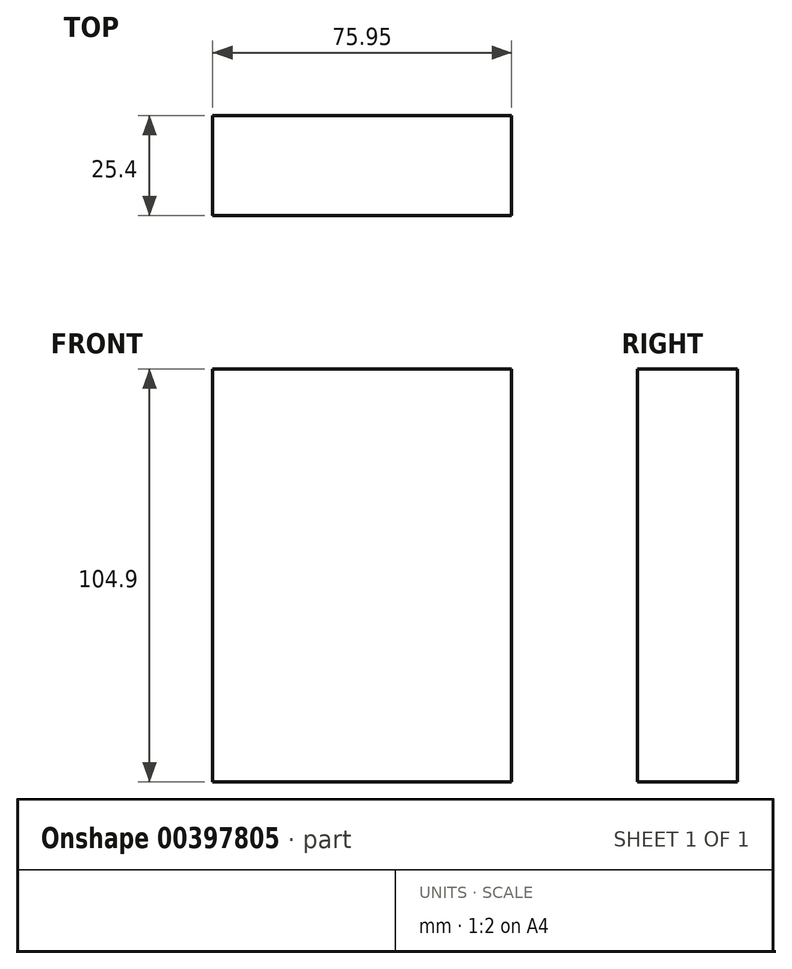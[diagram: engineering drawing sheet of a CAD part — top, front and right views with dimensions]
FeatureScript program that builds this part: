
annotation { "Feature Type Name" : "Feature", "Feature Type Description" : "" }
export const myFeature = defineFeature(function(context is Context, id is Id, definition is map)
    precondition{}
    {
        {
            var Q0;
            Q0=qCreatedBy(makeId("Front.planeOp"),FACE);
            var sketch = newSketch(context, id + "F0", { "sketchPlane" : qUnion([Q0])});
            skLineSegment(sketch, "E0", {"start": v(0, 0) * mm, "end": v(75.95, 0) * mm});
            skLineSegment(sketch, "E1", {"start": v(75.95, 0) * mm, "end": v(75.95, 57.52) * mm});
            skLineSegment(sketch, "E2", {"start": v(75.95, 57.52) * mm, "end": v(-68.21, 57.52) * mm});
            skLineSegment(sketch, "E3", {"start": v(-68.21, 57.52) * mm, "end": v(-68.21, -47.38) * mm});
            skLineSegment(sketch, "E4", {"start": v(-68.21, -47.38) * mm, "end": v(75.95, -47.38) * mm});
            skLineSegment(sketch, "E5", {"start": v(75.95, -47.38) * mm, "end": v(75.95, 0) * mm});
            skLineSegment(sketch, "E6", {"start": v(0, 0) * mm, "end": v(-68.21, 0) * mm});
            skLineSegment(sketch, "E7", {"start": v(-68.21, 0) * mm, "end": v(0, 0) * mm});
            skLineSegment(sketch, "E8", {"start": v(0, 57.52) * mm, "end": v(0, -47.38) * mm});
            skSolve(sketch);
        }
        {
            var Q0;
            {var subQ5=sQuery(id+"F0.wireOp",EDGE,"E7");Q0=makeQuery(id+"F0.imprint","IMPRINT",FACE,{"disambiguationData":[TD([[makeQuery(id+"F0.imprint","IMPRINT",EDGE,{"derivedFrom":subQ5}),1.0]])]});}
            var sketch = newSketch(context, id + "F1", { "sketchPlane" : qUnion([Q0])});
            skSolve(sketch);
        }
        {
            var Q0;
            Q0 = qSketchRegion(id + "F1", true);
            var Q1;
            {var subQ5=sQuery(id+"F0.wireOp",EDGE,"E7");Q1=makeQuery(id+"F0.imprint","IMPRINT",FACE,{"disambiguationData":[TD([[makeQuery(id+"F0.imprint","IMPRINT",EDGE,{"derivedFrom":subQ5}),1.0]])]});}
            var Q2;
            {var subQ0=sQuery(id+"F0.wireOp",EDGE,"E0");Q2=makeQuery(id+"F0.imprint","IMPRINT",FACE,{"disambiguationData":[TD([[makeQuery(id+"F0.imprint","IMPRINT",EDGE,{"derivedFrom":subQ0}),1.0]])]});}
            var Q3;
            {var subQ3=sQuery(id+"F0.wireOp",EDGE,"E7");Q3=makeQuery(id+"F0.imprint","IMPRINT",FACE,{"disambiguationData":[TD([[makeQuery(id+"F0.imprint","IMPRINT",EDGE,{"derivedFrom":subQ3}),-1.0]])]});}
            var Q4;
            {var subQ0=sQuery(id+"F0.wireOp",EDGE,"E0");Q4=makeQuery(id+"F0.imprint","IMPRINT",FACE,{"disambiguationData":[TD([[makeQuery(id+"F0.imprint","IMPRINT",EDGE,{"derivedFrom":subQ0}),-1.0]])]});}
            extrude(context, id + "F2", {"entities" : qUnion([Q0, Q1, Q2, Q3, Q4]), "depth" : 25.4 * mm});
        }
    });
